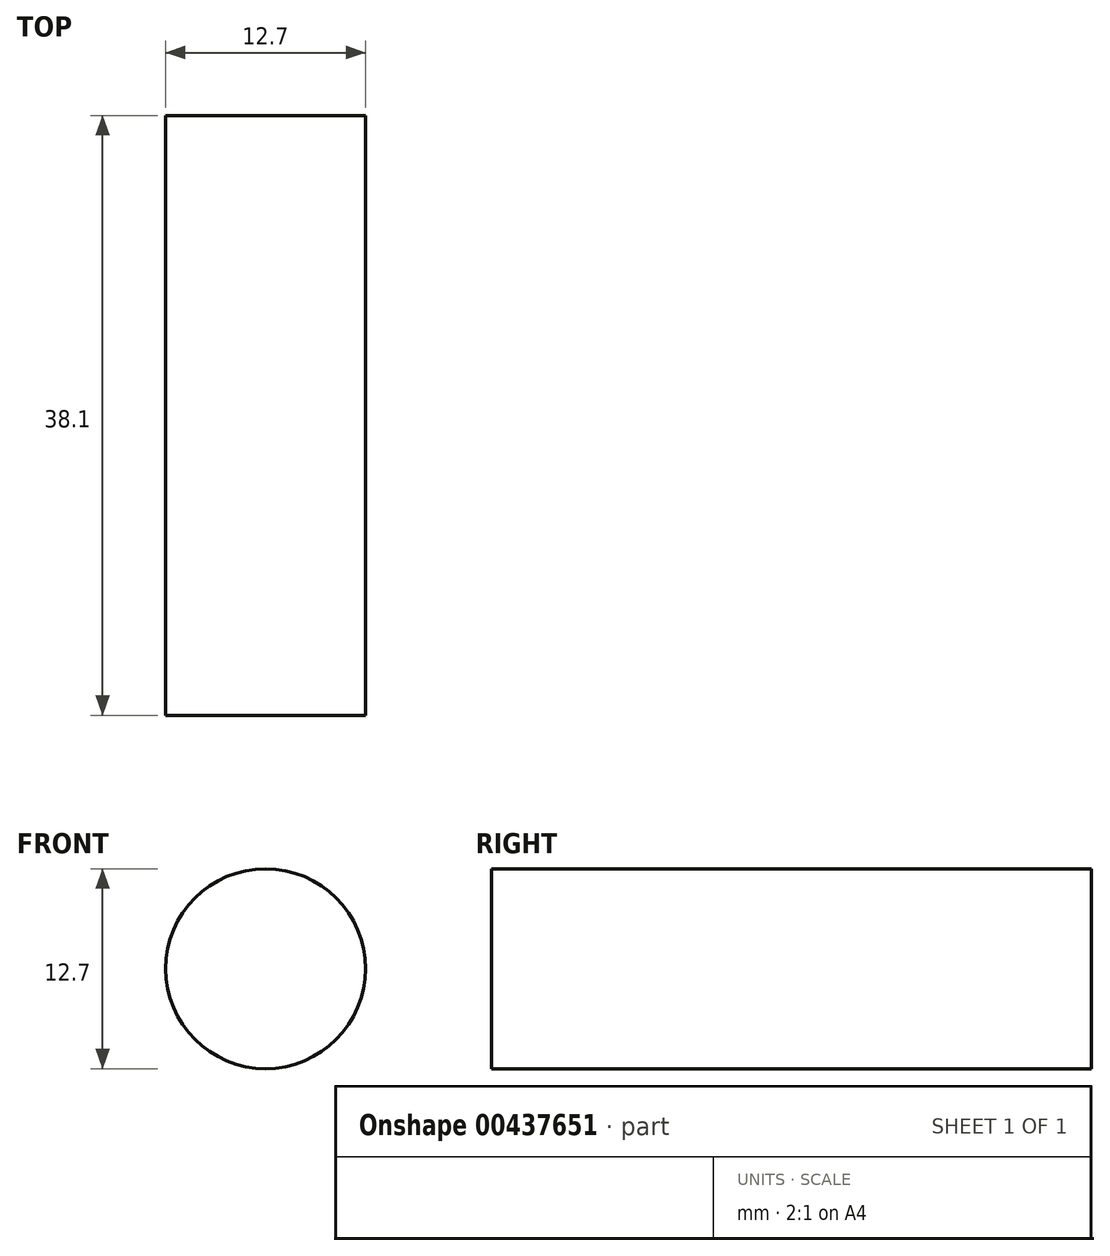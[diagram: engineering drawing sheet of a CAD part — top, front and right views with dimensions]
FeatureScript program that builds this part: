
annotation { "Feature Type Name" : "Feature", "Feature Type Description" : "" }
export const myFeature = defineFeature(function(context is Context, id is Id, definition is map)
    precondition{}
    {
        {
            var Q0;
            Q0=qCreatedBy(makeId("Front.planeOp"),FACE);
            var sketch = newSketch(context, id + "F0", { "sketchPlane" : qUnion([Q0])});
            skCircle(sketch, "E0", {"center": v(0, 0) * mm, "radius": 6.35 * mm});
            skSolve(sketch);
        }
        {
            var Q0;
            Q0 = qSketchRegion(id + "F0", true);
            extrude(context, id + "F1", {"entities" : qUnion([Q0]), "depth" : 38.1 * mm});
        }
    });
